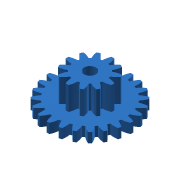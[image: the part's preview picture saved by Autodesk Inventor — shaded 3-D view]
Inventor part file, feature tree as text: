
AUTODESK INVENTOR PART (.ipt)
format: ipt  version: 2016 (Build 200138000, 138)  size: 346,624 bytes
history: native  units: mm (DEFAULTED — no unit token found)
features: sketch x5, extrude x4, other x4, plane x3
ambient origin geometry x8: Origin, YZ Plane, XZ Plane, XY Plane, X Axis, Y Axis, Z Axis, Center Point
bodies: Solid1 (feature_tree)
feature tree (16):
  extrude  "Extrusion1"  Depth=5.0mm TaperAngle=0.0deg
  plane  "Work Plane2"
  plane  "Work Plane8"
  plane  "Work Plane9"
  other  "Spur Gear"
  extrude  "Extrusion3"  Depth=10.0mm TaperAngle=0.0deg
  extrude  "Extrusion4"  Depth=1.308997mm TaperAngle=0.0deg
  extrude  "Extrusion5"  TaperAngle=0.0deg  [1 undecoded]
  sketch  "Sketch1"  dims[d0=43.066667mm d1=5.0mm d2=0.0mm]
  sketch  "Sketch2"  dims[d3=40.0mm d4=10.0mm d5=0.0mm]
  other  "Srf1"
  sketch  "Sketch6"  dims[d16=30.0mm d17=0.0mm d34=1.308997mm]
  sketch  "Sketch7"  dims[d39=0.0mm d41=0.0mm]
  sketch  "Sketch8"  dims[d43=30.0mm d46=30.0mm d47=0.0mm d48=0.0mm d52=23.646mm d53=12.0mm d54=0.0mm d55=240.0mm d56=120.0mm d57=10.0mm d58=0.0mm d59=0.0mm d60=20.0mm d61=16.086667mm d62=23.646106mm d63=20.32mm d64=0.0mm d65=12.0mm d66=30.0mm d67=120.0mm d68=360.0deg d69=120.0mm d70=360.0deg d71=120.0mm d72=360.0deg d73=0.0mm d74=12.0mm d75=6.1mm d76=20.0mm d77=0.0mm d78=30.0mm d79=2.0mm d80=0.0mm]
  other  "Pitch Diameter"
  other  "iFeature1:2"
note: 1 required parameter value undecoded (feature->parameter linkage not recoverable at this tier; creation-order binding heuristic only, values carry confidence <= 0.55)
